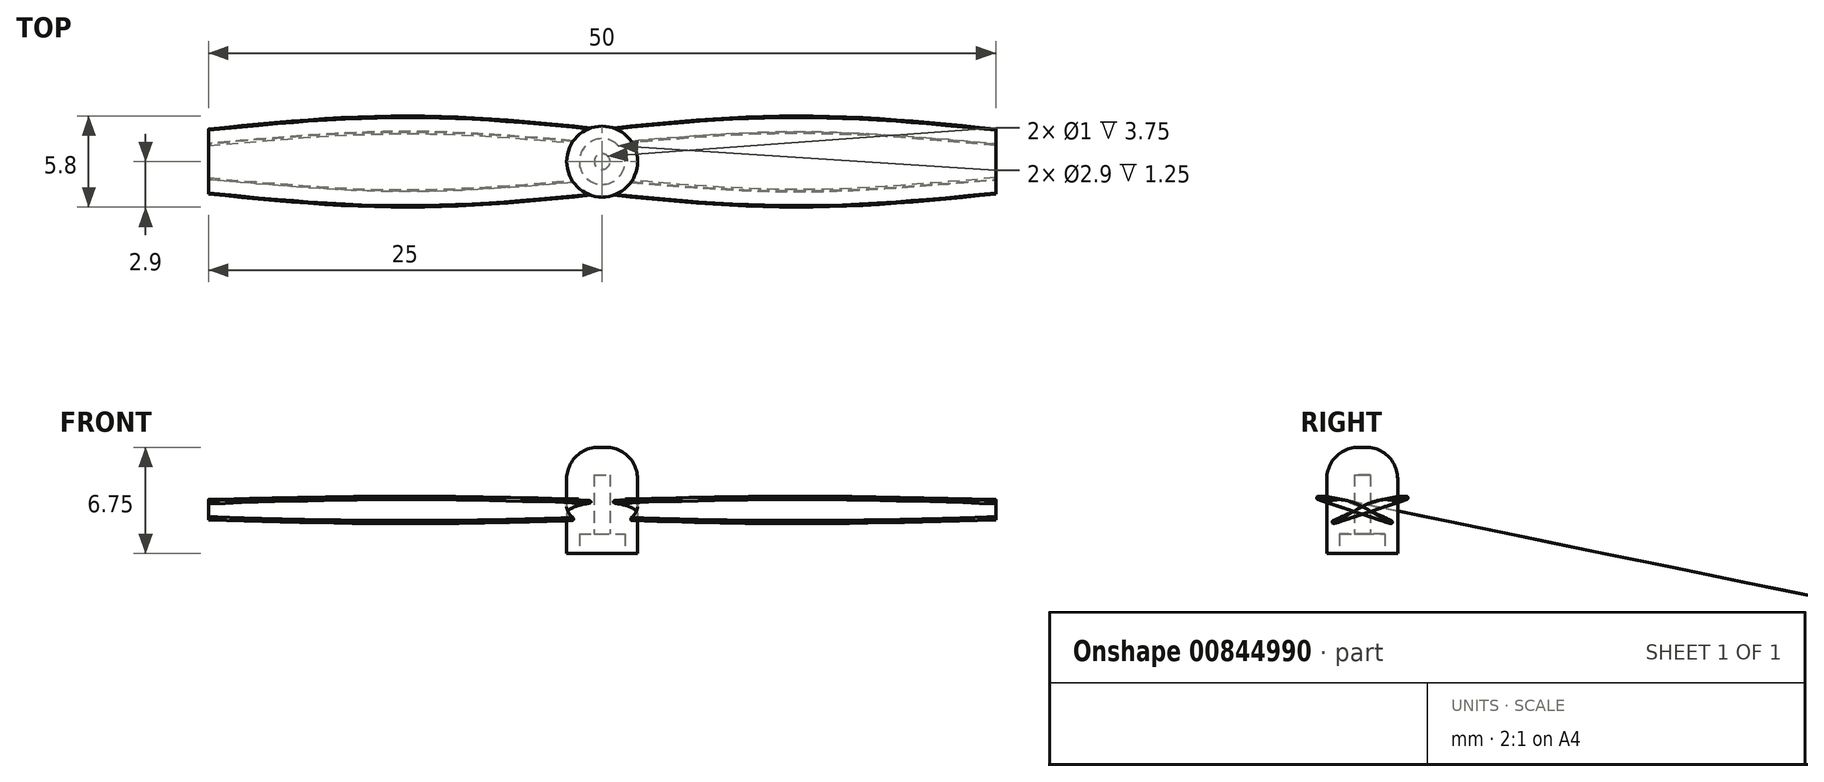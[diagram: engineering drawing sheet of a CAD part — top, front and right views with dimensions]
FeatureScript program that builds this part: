
annotation { "Feature Type Name" : "Feature", "Feature Type Description" : "" }
export const myFeature = defineFeature(function(context is Context, id is Id, definition is map)
    precondition{}
    {
        {
            var Q0;
            Q0=qCreatedBy(makeId("Top.planeOp"),FACE);
            var sketch = newSketch(context, id + "F0", { "sketchPlane" : qUnion([Q0])});
            skCircle(sketch, "E0", {"center": v(0, 0) * mm, "radius": 2.25 * mm});
            skCircle(sketch, "E1", {"center": v(0, 0) * mm, "radius": 1.45 * mm});
            skCircle(sketch, "E2", {"center": v(0, 0) * mm, "radius": 0.5 * mm});
            skSolve(sketch);
        }
        {
            var Q0;
            Q0=makeQuery(id+"F0.imprint","IMPRINT",FACE,{"disambiguationData":[TD([[makeQuery(id+"F0.imprint","IMPRINT",EDGE,{"derivedFrom":sQuery(id+"F0.wireOp",EDGE,"E0")}),1.0]])]});
            extrude(context, id + "F1", {"entities" : qUnion([Q0]), "depth" : 6.75 * mm, "offsetDistance" : 25 * mm});
        }
        {
            var Q0;
            Q0=makeQuery(id+"F0.imprint","IMPRINT",FACE,{"disambiguationData":[TD([[makeQuery(id+"F0.imprint","IMPRINT",EDGE,{"derivedFrom":sQuery(id+"F0.wireOp",EDGE,"E1")}),1.0]])]});
            extrude(context, id + "F2", {"entities" : qUnion([Q0]), "operationType" : NewBodyOperationType.ADD, "depth" : 6.75 * mm, "offsetDistance" : 25 * mm, "hasSecondDirection" : true, "secondDirectionOppositeDirection" : false, "secondDirectionDepth" : 1.25 * mm});
        }
        {
            var Q0;
            Q0=makeQuery(id+"F0.imprint","IMPRINT",FACE,{"disambiguationData":[TD([[makeQuery(id+"F0.imprint","IMPRINT",EDGE,{"derivedFrom":sQuery(id+"F0.wireOp",EDGE,"E2")}),1.0]])]});
            extrude(context, id + "F3", {"entities" : qUnion([Q0]), "operationType" : NewBodyOperationType.ADD, "depth" : 6.75 * mm, "offsetDistance" : 25 * mm, "hasSecondDirection" : true, "secondDirectionOppositeDirection" : false, "secondDirectionDepth" : 5 * mm});
        }
        {
            var Q0;
            Q0=makeQuery(id+"F1.opExtrude","CAP_EDGE",EDGE,{"disambiguationData":[OSD([sQuery(id+"F0.wireOp",EDGE,"E0")])],"isStart":false});
            fillet(context, id + "F4", {"entities" : qUnion([Q0]), "radius" : 2 * mm, "tangentPropagation" : true, "allowEdgeOverflow" : false});
        }
        {
            var Q0;
            Q0=qCreatedBy(makeId("Right.planeOp"),FACE);
            var sketch = newSketch(context, id + "F5", { "sketchPlane" : qUnion([Q0])});
            skLineSegment(sketch, "E3", {"start": v(2.25, 3.25) * mm, "end": v(-2.25, 1.75) * mm});
            skFitSpline(sketch, "E4", {"points": [v(2.25, 3.25) * mm, v(-2.25, 1.75) * mm], "startDerivative": vector(-4.5, 2.25) * mm, "endDerivative": vector(-3.75, -1.25) * mm});
            skSolve(sketch);
        }
        {
            var Q0;
            Q0=qCreatedBy(makeId("Right.planeOp"),FACE);
            cPlane(context, id + "F6", {"entities" : qUnion([Q0]), "cplaneType" : CPlaneType.OFFSET, "offset" : 12 * mm, "width" : 150 * mm, "height" : 150 * mm});
        }
        {
            var Q0;
            Q0=qCreatedBy(id+"F6.planeOp",FACE);
            var sketch = newSketch(context, id + "F7", { "sketchPlane" : qUnion([Q0])});
            skLineSegment(sketch, "E5", {"start": v(-3.88, 1.2) * mm, "end": v(3.24, 3.58) * mm});
            skFitSpline(sketch, "E6", {"points": [v(-3.88, 1.2) * mm, v(3.24, 3.58) * mm], "startDerivative": vector(7.12, 2.73) * mm, "endDerivative": vector(5.22, -1.26) * mm});
            skSolve(sketch);
        }
        {
            var Q0;
            Q0=qCreatedBy(makeId("Right.planeOp"),FACE);
            cPlane(context, id + "F8", {"entities" : qUnion([Q0]), "cplaneType" : CPlaneType.OFFSET, "offset" : 25 * mm, "width" : 150 * mm, "height" : 150 * mm});
        }
        {
            var Q0;
            Q0=qCreatedBy(id+"F8.planeOp",FACE);
            var sketch = newSketch(context, id + "F9", { "sketchPlane" : qUnion([Q0])});
            skLineSegment(sketch, "E7", {"start": v(-2.25, 1.75) * mm, "end": v(2.25, 3.25) * mm});
            skFitSpline(sketch, "E8", {"points": [v(-2.25, 1.75) * mm, v(2.25, 3.25) * mm], "startDerivative": vector(3.75, 1.25) * mm, "endDerivative": vector(4.5, -2.25) * mm});
            skSolve(sketch);
        }
        {
            var Q1;
            Q1=makeQuery(id+"F5.imprint","IMPRINT",FACE,{"disambiguationData":[TD([[makeQuery(id+"F5.imprint","IMPRINT",EDGE,{"derivedFrom":sQuery(id+"F5.wireOp",EDGE,"E3")}),-1.0]])]});
            var Q2;
            Q2=makeQuery(id+"F7.imprint","IMPRINT",FACE,{"disambiguationData":[TD([[makeQuery(id+"F7.imprint","IMPRINT",EDGE,{"derivedFrom":sQuery(id+"F7.wireOp",EDGE,"E5")}),1.0]])]});
            var Q3;
            Q3=makeQuery(id+"F9.imprint","IMPRINT",FACE,{"disambiguationData":[TD([[makeQuery(id+"F9.imprint","IMPRINT",EDGE,{"derivedFrom":sQuery(id+"F9.wireOp",EDGE,"E7")}),1.0]])]});
            loft(context, id + "F10", {"sheetProfilesArray" : [{ "sheetProfileEntities" : qUnion([Q1]) }, { "sheetProfileEntities" : qUnion([Q2]) }, { "sheetProfileEntities" : qUnion([Q3]) }]});
        }
        {
            var Q0;
            {var subQ0=sQuery(id+"F7.wireOp",EDGE,"E6");var subQ1=sQuery(id+"F7.wireOp",EDGE,"E5");var subQ2=sQuery(id+"F5.wireOp",EDGE,"E4");var subQ3=sQuery(id+"F5.wireOp",EDGE,"E3");Q0=makeQuery(id+"F10.opLoft","SWEPT_EDGE",EDGE,{"disambiguationData":[OSD([subQ3,subQ2,subQ1,subQ0]),TDD([makeQuery(id+"F5.imprint","INTERSECT",VERTEX,{"disambiguationData":[OD(1.0)],"derivedFrom":[subQ3,subQ2]}),makeQuery(id+"F7.imprint","INTERSECT",VERTEX,{"disambiguationData":[OD(0.0)],"derivedFrom":[subQ1,subQ0]})])]});}
            var Q1;
            {var subQ0=sQuery(id+"F7.wireOp",EDGE,"E6");var subQ1=sQuery(id+"F7.wireOp",EDGE,"E5");var subQ2=sQuery(id+"F5.wireOp",EDGE,"E4");var subQ3=sQuery(id+"F5.wireOp",EDGE,"E3");Q1=makeQuery(id+"F10.opLoft","SWEPT_EDGE",EDGE,{"disambiguationData":[OSD([subQ3,subQ2,subQ1,subQ0]),TDD([makeQuery(id+"F5.imprint","INTERSECT",VERTEX,{"disambiguationData":[OD(0.0)],"derivedFrom":[subQ3,subQ2]}),makeQuery(id+"F7.imprint","INTERSECT",VERTEX,{"disambiguationData":[OD(1.0)],"derivedFrom":[subQ1,subQ0]})])]});}
            fillet(context, id + "F11", {"entities" : qUnion([Q0, Q1]), "radius" : .1 * mm, "tangentPropagation" : true, "allowEdgeOverflow" : false});
        }
        {
            var Q0;
            Q0=makeQuery(id+"F10.opLoft","SWEPT_BODY",BODY,{"disambiguationData":[OSD([makeQuery(id+"F5.imprint","IMPRINT",FACE,{"disambiguationData":[TD([[makeQuery(id+"F5.imprint","IMPRINT",EDGE,{"derivedFrom":sQuery(id+"F5.wireOp",EDGE,"E3")}),-1.0]])]}),sQuery(id+"F7.wireOp",EDGE,"E6"),makeQuery(id+"F9.imprint","IMPRINT",FACE,{"disambiguationData":[TD([[makeQuery(id+"F9.imprint","IMPRINT",EDGE,{"derivedFrom":sQuery(id+"F9.wireOp",EDGE,"E7")}),1.0]])]})])]});
            var Q1;
            Q1=sQuery(id+"F0.wireOp",EDGE,"E0");
            circularPattern(context, id + "F12", {"operationType" : NewBodyOperationType.ADD, "entities" : qUnion([Q0]), "axis" : qUnion([Q1]), "angle" : 360 * degree, "instanceCount" : 2, "equalSpace" : true});
        }
        {
            var Q0;
            Q0=makeQuery(id+"F0.imprint","IMPRINT",FACE,{"disambiguationData":[TD([[makeQuery(id+"F0.imprint","IMPRINT",EDGE,{"derivedFrom":sQuery(id+"F0.wireOp",EDGE,"E2")}),1.0]])]});
            extrude(context, id + "F13", {"entities" : qUnion([Q0]), "operationType" : NewBodyOperationType.REMOVE, "depth" : 5 * mm, "offsetDistance" : 25 * mm});
        }
        {
            var Q0;
            Q0=makeQuery(id+"F1.opExtrude","SWEPT_BODY",BODY,{"disambiguationData":[OSD([sQuery(id+"F0.wireOp",EDGE,"E0"),sQuery(id+"F0.wireOp",EDGE,"E1")])]});
            var Q1;
            Q1=qCreatedBy(makeId("Right.planeOp"),FACE);
            mirror(context, id + "F14", {"entities" : qUnion([Q0]), "mirrorPlane" : qUnion([Q1])});
        }
    });
